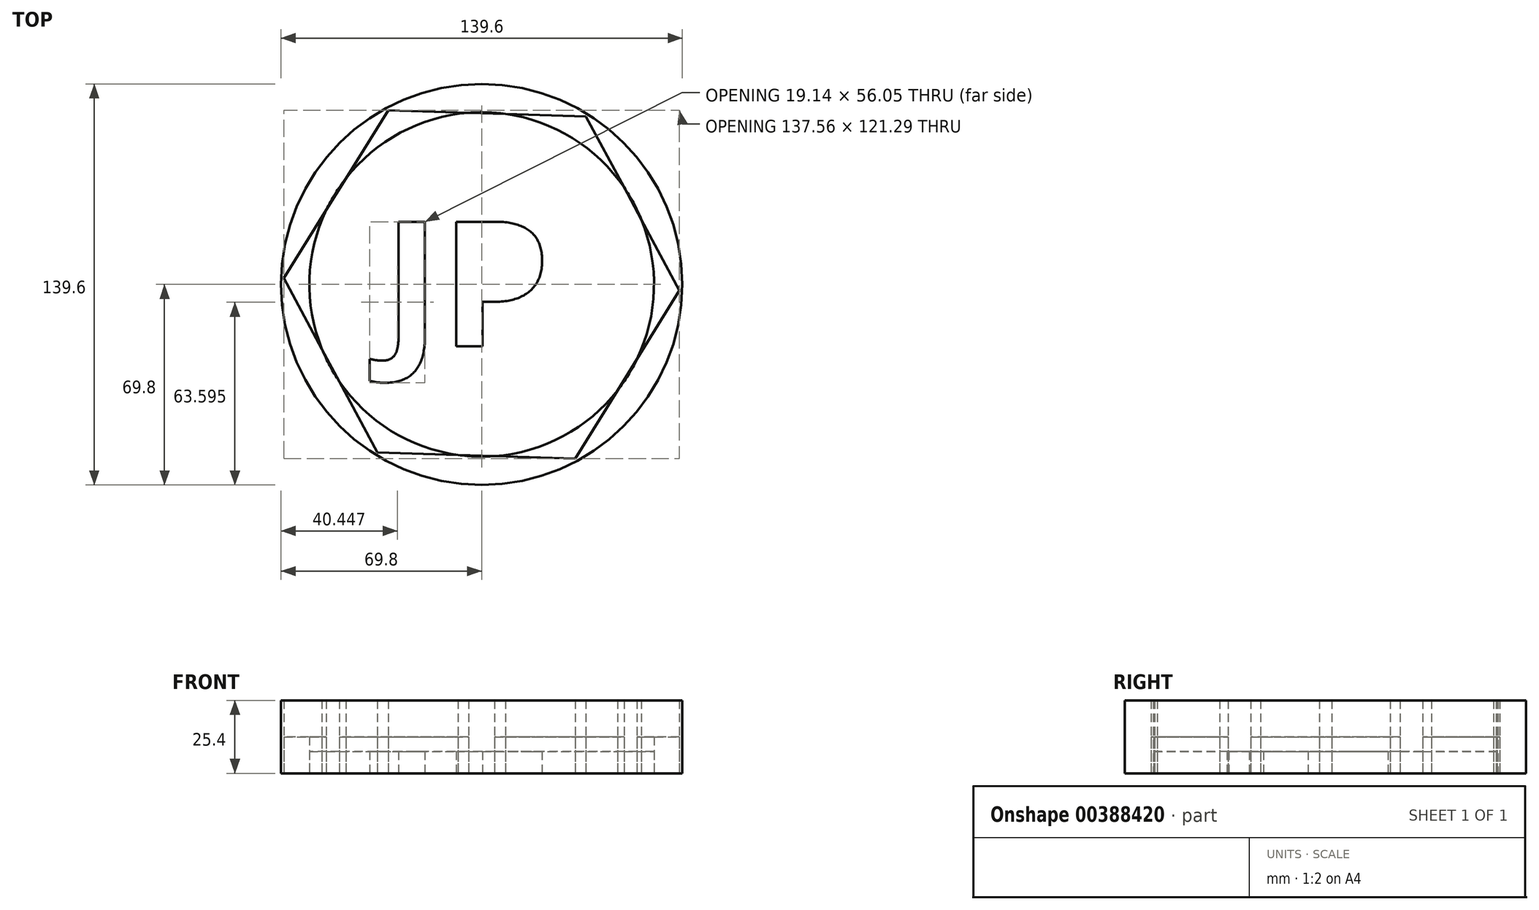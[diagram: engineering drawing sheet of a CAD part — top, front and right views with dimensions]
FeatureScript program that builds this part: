
annotation { "Feature Type Name" : "Feature", "Feature Type Description" : "" }
export const myFeature = defineFeature(function(context is Context, id is Id, definition is map)
    precondition{}
    {
        {
            var Q0;
            Q0=qCreatedBy(makeId("Top.planeOp"),FACE);
            var sketch = newSketch(context, id + "F0", { "sketchPlane" : qUnion([Q0])});
            skCircle(sketch, "E0", {"center": v(0, 0) * mm, "radius": 69.8 * mm});
            skLineSegment(sketch, "E1.0", {"start": v(36.26, 58.49) * mm, "end": v(68.78, -2.16) * mm});
            skLineSegment(sketch, "E1.1", {"start": v(68.78, -2.16) * mm, "end": v(32.52, -60.65) * mm});
            skLineSegment(sketch, "E1.2", {"start": v(32.52, -60.65) * mm, "end": v(-36.26, -58.49) * mm});
            skLineSegment(sketch, "E1.3", {"start": v(-36.26, -58.49) * mm, "end": v(-68.78, 2.16) * mm});
            skLineSegment(sketch, "E1.4", {"start": v(-68.78, 2.16) * mm, "end": v(-32.52, 60.65) * mm});
            skLineSegment(sketch, "E1.5", {"start": v(-32.52, 60.65) * mm, "end": v(36.26, 58.49) * mm});
            skPoint(sketch, "E1.0.midPoint", {"position": v(52.52, 28.16) * mm});
            skText(sketch, "E2", { "text": "JP", "fontName": "OpenSans-Bold.ttf"});
            skCircle(sketch, "E3", {"center": v(0, 0) * mm, "radius": 59.94 * mm});
            const initialGuessF0  = {"E2": [-0.03442, -0.02149, 1, 0, 0.04368]};
            skSetInitialGuess(sketch, initialGuessF0);
            skSolve(sketch);
        }
        {
            var Q0;
            Q0=makeQuery(id+"F0.imprint","IMPRINT",FACE,{"disambiguationData":[TD([[makeQuery(id+"F0.imprint","IMPRINT",EDGE,{"derivedFrom":sQuery(id+"F0.wireOp",EDGE,"E0")}),1.0]])]});
            extrude(context, id + "F1", {"entities" : qUnion([Q0]), "depth" : 25.4 * mm});
        }
        {
            var Q0;
            {var subQ0=sQuery(id+"F0.wireOp",EDGE,"E1.4");var subQ1=sQuery(id+"F0.wireOp",EDGE,"E1.3");var subQ2=makeQuery(id+"F0.imprint","INTERSECT",VERTEX,{"derivedFrom":[subQ1,subQ0]});Q0=makeQuery(id+"F0.imprint","IMPRINT",FACE,{"disambiguationData":[TD([[makeQuery(id+"F0.imprint","IMPRINT",EDGE,{"disambiguationData":[TD([[subQ2,1.0]])],"derivedFrom":subQ1}),-1.0]])]});}
            var Q1;
            {var subQ0=sQuery(id+"F0.wireOp",EDGE,"E1.3");var subQ1=sQuery(id+"F0.wireOp",EDGE,"E1.2");var subQ2=makeQuery(id+"F0.imprint","INTERSECT",VERTEX,{"derivedFrom":[subQ1,subQ0]});Q1=makeQuery(id+"F0.imprint","IMPRINT",FACE,{"disambiguationData":[TD([[makeQuery(id+"F0.imprint","IMPRINT",EDGE,{"disambiguationData":[TD([[subQ2,1.0]])],"derivedFrom":subQ1}),-1.0]])]});}
            var Q2;
            {var subQ0=sQuery(id+"F0.wireOp",EDGE,"E1.5");var subQ1=sQuery(id+"F0.wireOp",EDGE,"E1.4");var subQ2=makeQuery(id+"F0.imprint","INTERSECT",VERTEX,{"derivedFrom":[subQ1,subQ0]});Q2=makeQuery(id+"F0.imprint","IMPRINT",FACE,{"disambiguationData":[TD([[makeQuery(id+"F0.imprint","IMPRINT",EDGE,{"disambiguationData":[TD([[subQ2,1.0]])],"derivedFrom":subQ1}),-1.0]])]});}
            var Q3;
            {var subQ0=sQuery(id+"F0.wireOp",EDGE,"E1.5");var subQ1=sQuery(id+"F0.wireOp",EDGE,"E1.0");var subQ2=makeQuery(id+"F0.imprint","INTERSECT",VERTEX,{"derivedFrom":[subQ1,subQ0]});Q3=makeQuery(id+"F0.imprint","IMPRINT",FACE,{"disambiguationData":[TD([[makeQuery(id+"F0.imprint","IMPRINT",EDGE,{"disambiguationData":[TD([[subQ2,-1.0]])],"derivedFrom":subQ1}),-1.0]])]});}
            var Q4;
            {var subQ0=sQuery(id+"F0.wireOp",EDGE,"E1.1");var subQ1=sQuery(id+"F0.wireOp",EDGE,"E1.0");var subQ2=makeQuery(id+"F0.imprint","INTERSECT",VERTEX,{"derivedFrom":[subQ1,subQ0]});Q4=makeQuery(id+"F0.imprint","IMPRINT",FACE,{"disambiguationData":[TD([[makeQuery(id+"F0.imprint","IMPRINT",EDGE,{"disambiguationData":[TD([[subQ2,1.0]])],"derivedFrom":subQ1}),-1.0]])]});}
            var Q5;
            {var subQ0=sQuery(id+"F0.wireOp",EDGE,"E1.2");var subQ1=sQuery(id+"F0.wireOp",EDGE,"E1.1");var subQ2=makeQuery(id+"F0.imprint","INTERSECT",VERTEX,{"derivedFrom":[subQ1,subQ0]});Q5=makeQuery(id+"F0.imprint","IMPRINT",FACE,{"disambiguationData":[TD([[makeQuery(id+"F0.imprint","IMPRINT",EDGE,{"disambiguationData":[TD([[subQ2,1.0]])],"derivedFrom":subQ1}),-1.0]])]});}
            extrude(context, id + "F2", {"entities" : qUnion([Q0, Q1, Q2, Q3, Q4, Q5]), "depth" : 12.7 * mm});
        }
        {
            var Q0;
            Q0=makeQuery(id+"F0.imprint","IMPRINT",FACE,{"disambiguationData":[TD([[makeQuery(id+"F0.imprint","IMPRINT",EDGE,{"derivedFrom":sQuery(id+"F0.wireOp",EDGE,"E2.sketch_text.stroke-0")}),1.0]])]});
            extrude(context, id + "F3", {"entities" : qUnion([Q0]), "depth" : 7.62 * mm});
        }
    });
